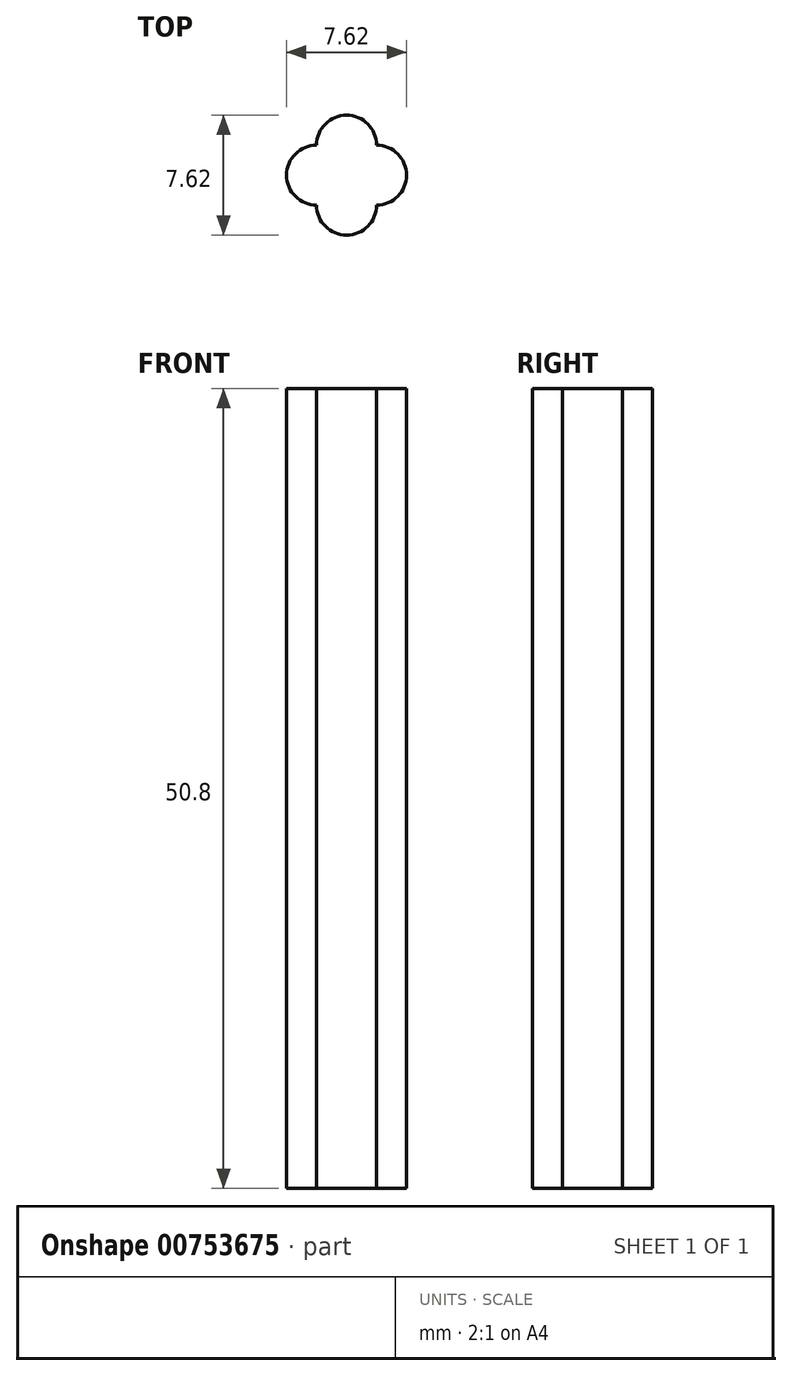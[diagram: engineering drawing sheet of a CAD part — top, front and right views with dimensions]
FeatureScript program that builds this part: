
annotation { "Feature Type Name" : "Feature", "Feature Type Description" : "" }
export const myFeature = defineFeature(function(context is Context, id is Id, definition is map)
    precondition{}
    {
        {
            var Q0;
            Q0=qCreatedBy(makeId("Top.planeOp"),FACE);
            var sketch = newSketch(context, id + "F0", { "sketchPlane" : qUnion([Q0])});
            skLineSegment(sketch, "E0.bottom", {"start": v(-1.66, 4.61) * mm, "end": v(2.15, 4.61) * mm});
            skLineSegment(sketch, "E0.top", {"start": v(-1.66, 0.8) * mm, "end": v(2.15, 0.8) * mm});
            skLineSegment(sketch, "E0.left", {"start": v(-1.66, 4.61) * mm, "end": v(-1.66, 0.8) * mm});
            skLineSegment(sketch, "E0.right", {"start": v(2.15, 4.61) * mm, "end": v(2.15, 0.8) * mm});
            skArc(sketch, "E1", {"start": v(2.15, 4.61) * mm, "mid": v(0.24, 6.52) * mm, "end": v(-1.66, 4.61) * mm});
            skArc(sketch, "E2", {"start": v(2.15, 0.8) * mm, "mid": v(4.05, 2.7) * mm, "end": v(2.15, 4.61) * mm});
            skArc(sketch, "E3", {"start": v(-1.66, 0.8) * mm, "mid": v(0.24, -1.1) * mm, "end": v(2.15, 0.8) * mm});
            skArc(sketch, "E4", {"start": v(-1.66, 4.61) * mm, "mid": v(-3.57, 2.7) * mm, "end": v(-1.66, 0.8) * mm});
            skSolve(sketch);
        }
        {
            var Q0;
            Q0=makeQuery(id+"F0.imprint","IMPRINT",FACE,{"disambiguationData":[TD([[makeQuery(id+"F0.imprint","IMPRINT",EDGE,{"derivedFrom":sQuery(id+"F0.wireOp",EDGE,"E0.bottom")}),1.0]])]});
            var Q1;
            Q1=makeQuery(id+"F0.imprint","IMPRINT",FACE,{"disambiguationData":[TD([[makeQuery(id+"F0.imprint","IMPRINT",EDGE,{"derivedFrom":sQuery(id+"F0.wireOp",EDGE,"E0.top")}),-1.0]])]});
            var Q2;
            Q2=makeQuery(id+"F0.imprint","IMPRINT",FACE,{"disambiguationData":[TD([[makeQuery(id+"F0.imprint","IMPRINT",EDGE,{"derivedFrom":sQuery(id+"F0.wireOp",EDGE,"E0.left")}),-1.0]])]});
            var Q3;
            Q3=makeQuery(id+"F0.imprint","IMPRINT",FACE,{"disambiguationData":[TD([[makeQuery(id+"F0.imprint","IMPRINT",EDGE,{"derivedFrom":sQuery(id+"F0.wireOp",EDGE,"E0.bottom")}),-1.0]])]});
            var Q4;
            Q4=makeQuery(id+"F0.imprint","IMPRINT",FACE,{"disambiguationData":[TD([[makeQuery(id+"F0.imprint","IMPRINT",EDGE,{"derivedFrom":sQuery(id+"F0.wireOp",EDGE,"E0.right")}),1.0]])]});
            extrude(context, id + "F1", {"entities" : qUnion([Q0, Q1, Q2, Q3, Q4]), "depth" : 50.8 * mm, "offsetDistance" : 25.4 * mm});
        }
    });
